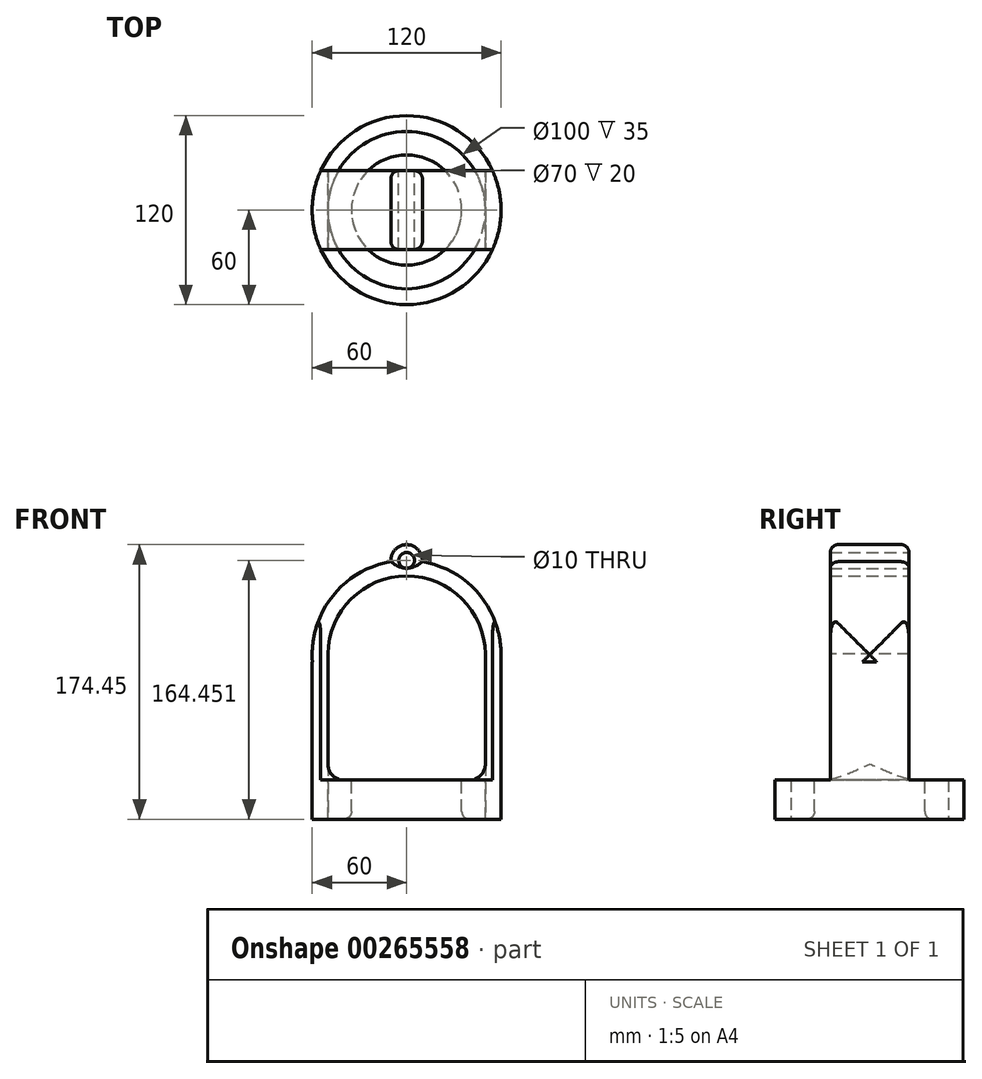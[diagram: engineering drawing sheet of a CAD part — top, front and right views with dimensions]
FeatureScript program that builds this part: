
annotation { "Feature Type Name" : "Feature", "Feature Type Description" : "" }
export const myFeature = defineFeature(function(context is Context, id is Id, definition is map)
    precondition{}
    {
        {
            var Q0;
            Q0=qCreatedBy(makeId("Top.planeOp"),FACE);
            var sketch = newSketch(context, id + "F0", { "sketchPlane" : qUnion([Q0])});
            skCircle(sketch, "E0", {"center": v(0, 0) * mm, "radius": 35 * mm});
            skCircle(sketch, "E1", {"center": v(0, 0) * mm, "radius": 50 * mm});
            skCircle(sketch, "E2", {"center": v(0, 0) * mm, "radius": 60 * mm});
            skCircle(sketch, "E3", {"center": v(0, 0) * mm, "radius": 78.9 * mm});
            skSolve(sketch);
        }
        {
            var Q0;
            Q0=qCreatedBy(makeId("Front.planeOp"),FACE);
            var sketch = newSketch(context, id + "F1", { "sketchPlane" : qUnion([Q0])});
            skLineSegment(sketch, "E4.bottom", {"start": v(-40, 0) * mm, "end": v(40, 0) * mm});
            skLineSegment(sketch, "E4.top", {"start": v(-50, 80) * mm, "end": v(50, 80) * mm});
            skLineSegment(sketch, "E4.left", {"start": v(-50, 10) * mm, "end": v(-50, 80) * mm});
            skLineSegment(sketch, "E4.right", {"start": v(50, 10) * mm, "end": v(50, 80) * mm});
            skPoint(sketch, "E5.visualSharp", {"position": v(-50, 0) * mm});
            skArc(sketch, "E5.filletArc", {"start": v(-50, 10) * mm, "mid": v(-47.07, 2.93) * mm, "end": v(-40, 0) * mm});
            skPoint(sketch, "E6.visualSharp", {"position": v(50, 0) * mm});
            skArc(sketch, "E6.filletArc", {"start": v(40, 0) * mm, "mid": v(47.07, 2.93) * mm, "end": v(50, 10) * mm});
            skPoint(sketch, "E7", {"position": v(0, 0) * mm});
            skPoint(sketch, "E8", {"position": v(0, 80) * mm});
            skSolve(sketch);
        }
        {
            var Q0;
            Q0=qCreatedBy(makeId("Front.planeOp"),FACE);
            var sketch = newSketch(context, id + "F2", { "sketchPlane" : qUnion([Q0])});
            skCircle(sketch, "E9", {"center": v(0, 79.45) * mm, "radius": 50 * mm});
            skCircle(sketch, "E10", {"center": v(0, 79.45) * mm, "radius": 60 * mm});
            skCircle(sketch, "E11", {"center": v(0, 139.45) * mm, "radius": 10 * mm});
            skCircle(sketch, "E12", {"center": v(0, 139.45) * mm, "radius": 5 * mm});
            skSolve(sketch);
        }
        {
            var Q0;
            Q0=qCreatedBy(makeId("Right.planeOp"),FACE);
            var sketch = newSketch(context, id + "F3", { "sketchPlane" : qUnion([Q0])});
            skLineSegment(sketch, "E13.bottom", {"start": v(-25, 75) * mm, "end": v(-65, 75) * mm});
            skLineSegment(sketch, "E13.top", {"start": v(-25, 0) * mm, "end": v(-65, 0) * mm});
            skLineSegment(sketch, "E13.left", {"start": v(-25, 75) * mm, "end": v(-25, 0) * mm});
            skLineSegment(sketch, "E13.right", {"start": v(-65, 75) * mm, "end": v(-65, 0) * mm});
            skLineSegment(sketch, "E14.bottom", {"start": v(65, 75) * mm, "end": v(25, 75) * mm});
            skLineSegment(sketch, "E14.top", {"start": v(65, 0) * mm, "end": v(25, 0) * mm});
            skLineSegment(sketch, "E14.left", {"start": v(65, 75) * mm, "end": v(65, 0) * mm});
            skLineSegment(sketch, "E14.right", {"start": v(25, 75) * mm, "end": v(25, 0) * mm});
            skSolve(sketch);
        }
        {
            var Q0;
            Q0=makeQuery(id+"F0.imprint","IMPRINT",FACE,{"disambiguationData":[TD([[makeQuery(id+"F0.imprint","IMPRINT",EDGE,{"derivedFrom":sQuery(id+"F0.wireOp",EDGE,"E1")}),-1.0]])]});
            extrude(context, id + "F4", {"entities" : qUnion([Q0]), "depth" : 75 * mm, "hasSecondDirection" : true, "secondDirectionOppositeDirection" : true, "secondDirectionDepth" : 25 * mm});
        }
        {
            var Q0;
            Q0=makeQuery(id+"F0.imprint","IMPRINT",FACE,{"disambiguationData":[TD([[makeQuery(id+"F0.imprint","IMPRINT",EDGE,{"derivedFrom":sQuery(id+"F0.wireOp",EDGE,"E0")}),-1.0]])]});
            extrude(context, id + "F5", {"entities" : qUnion([Q0]), "oppositeDirection" : true, "depth" : 25 * mm});
        }
        {
            var Q0;
            Q0 = qSketchRegion(id + "F1", true);
            extrude(context, id + "F6", {"entities" : qUnion([Q0]), "depth" : 25 * mm});
        }
        {
            var Q0;
            Q0=makeQuery(id+"F2.imprint","IMPRINT",FACE,{"disambiguationData":[TD([[makeQuery(id+"F2.imprint","IMPRINT",EDGE,{"derivedFrom":sQuery(id+"F2.wireOp",EDGE,"E9")}),-1.0]])]});
            var Q1;
            {var subQ0=sQuery(id+"F2.wireOp",EDGE,"E11");var subQ2=sQuery(id+"F2.wireOp",EDGE,"E10");var subQ4=makeQuery(id+"F2.imprint","INTERSECT",VERTEX,{"disambiguationData":[OD(0.0)],"derivedFrom":[subQ2,subQ0]});Q1=makeQuery(id+"F2.imprint","IMPRINT",FACE,{"disambiguationData":[TD([[makeQuery(id+"F2.imprint","IMPRINT",EDGE,{"disambiguationData":[TD([[subQ4,-1.0]])],"derivedFrom":subQ2}),1.0]])]});}
            var Q2;
            {var subQ0=sQuery(id+"F2.wireOp",EDGE,"E11");var subQ1=sQuery(id+"F2.wireOp",EDGE,"E10");var subQ2=makeQuery(id+"F2.imprint","INTERSECT",VERTEX,{"disambiguationData":[OD(0.0)],"derivedFrom":[subQ1,subQ0]});Q2=makeQuery(id+"F2.imprint","IMPRINT",FACE,{"disambiguationData":[TD([[makeQuery(id+"F2.imprint","IMPRINT",EDGE,{"disambiguationData":[TD([[subQ2,-1.0]])],"derivedFrom":subQ1}),-1.0]])]});}
            extrude(context, id + "F7", {"entities" : qUnion([Q0, Q1, Q2]), "operationType" : NewBodyOperationType.ADD, "depth" : 25 * mm, "hasSecondDirection" : true, "secondDirectionOppositeDirection" : true, "secondDirectionDepth" : 25 * mm});
        }
        {
            var Q0;
            Q0 = qSketchRegion(id + "F1", true);
            extrude(context, id + "F8", {"entities" : qUnion([Q0]), "operationType" : NewBodyOperationType.REMOVE, "oppositeDirection" : true, "depth" : 100 * mm, "hasSecondDirection" : true, "secondDirectionOppositeDirection" : false, "secondDirectionDepth" : 100 * mm});
        }
        {
            var Q0;
            Q0=makeQuery(id+"F0.imprint","IMPRINT",FACE,{"disambiguationData":[TD([[makeQuery(id+"F0.imprint","IMPRINT",EDGE,{"derivedFrom":sQuery(id+"F0.wireOp",EDGE,"E2")}),-1.0]])]});
            extrude(context, id + "F9", {"entities" : qUnion([Q0]), "operationType" : NewBodyOperationType.REMOVE, "depth" : 150 * mm});
        }
        {
            var Q0;
            Q0 = qSketchRegion(id + "F3", true);
            extrude(context, id + "F10", {"entities" : qUnion([Q0]), "operationType" : NewBodyOperationType.REMOVE, "oppositeDirection" : true, "depth" : 100 * mm, "hasSecondDirection" : true, "secondDirectionOppositeDirection" : false, "secondDirectionDepth" : 100 * mm});
        }
        {
            var Q0;
            Q0=makeQuery(id+"F7.boolean.opBoolean","SPLIT",EDGE,{"disambiguationData":[OD(0.0)],"derivedFrom":makeQuery(id+"F7.opExtrude","CAP_EDGE",EDGE,{"disambiguationData":[OSD([sQuery(id+"F2.wireOp",EDGE,"E10")])],"isStart":false})});
            var Q1;
            Q1=makeQuery(id+"F7.boolean.opBoolean","SPLIT",EDGE,{"disambiguationData":[OD(1.0)],"derivedFrom":makeQuery(id+"F7.opExtrude","CAP_EDGE",EDGE,{"disambiguationData":[OSD([sQuery(id+"F2.wireOp",EDGE,"E10")])],"isStart":false})});
            fillet(context, id + "F11", {"entities" : qUnion([Q0, Q1]), "radius" : 5 * mm, "tangentPropagation" : true, "allowEdgeOverflow" : false});
        }
        {
            var Q0;
            Q0=makeQuery(id+"F5.opExtrude","CAP_EDGE",EDGE,{"disambiguationData":[OSD([sQuery(id+"F0.wireOp",EDGE,"E0")])],"isStart":false});
            fillet(context, id + "F12", {"entities" : qUnion([Q0]), "radius" : 5 * mm, "tangentPropagation" : true, "allowEdgeOverflow" : false});
        }
        {
            var Q0;
            {var subQ0=sQuery(id+"F2.wireOp",EDGE,"E11");var subQ1=sQuery(id+"F2.wireOp",EDGE,"E10");Q0=makeQuery(id+"F7.boolean.opBoolean","SPLIT",EDGE,{"disambiguationData":[TD([makeQuery(id+"F4.opExtrude","SWEPT_FACE",FACE,{"disambiguationData":[OSD([sQuery(id+"F0.wireOp",EDGE,"E2")])]}),makeQuery(id+"F7.opExtrude","CAP_FACE",FACE,{"disambiguationData":[OSD([sQuery(id+"F2.wireOp",EDGE,"E9"),subQ1,subQ0,sQuery(id+"F2.wireOp",EDGE,"E12")])],"isStart":true}),makeQuery(id+"F7.opExtrude","SWEPT_FACE",FACE,{"disambiguationData":[OSD([subQ1])]}),makeQuery(id+"F7.opExtrude","SWEPT_FACE",FACE,{"disambiguationData":[OSD([subQ0])]})]),OD(1.0)],"derivedFrom":makeQuery(id+"F7.opExtrude","CAP_EDGE",EDGE,{"disambiguationData":[OSD([subQ1])],"isStart":true})});}
            var Q1;
            {var subQ0=sQuery(id+"F2.wireOp",EDGE,"E11");var subQ1=sQuery(id+"F2.wireOp",EDGE,"E10");Q1=makeQuery(id+"F7.boolean.opBoolean","SPLIT",EDGE,{"disambiguationData":[TD([makeQuery(id+"F4.opExtrude","SWEPT_FACE",FACE,{"disambiguationData":[OSD([sQuery(id+"F0.wireOp",EDGE,"E2")])]}),makeQuery(id+"F7.opExtrude","CAP_FACE",FACE,{"disambiguationData":[OSD([sQuery(id+"F2.wireOp",EDGE,"E9"),subQ1,subQ0,sQuery(id+"F2.wireOp",EDGE,"E12")])],"isStart":true}),makeQuery(id+"F7.opExtrude","SWEPT_FACE",FACE,{"disambiguationData":[OSD([subQ1])]}),makeQuery(id+"F7.opExtrude","SWEPT_FACE",FACE,{"disambiguationData":[OSD([subQ0])]})]),OD(0.0)],"derivedFrom":makeQuery(id+"F7.opExtrude","CAP_EDGE",EDGE,{"disambiguationData":[OSD([subQ1])],"isStart":true})});}
            var Q2;
            Q2=makeQuery(id+"F7.opExtrude","CAP_EDGE",EDGE,{"disambiguationData":[OSD([sQuery(id+"F2.wireOp",EDGE,"E11")])],"isStart":true});
            var Q3;
            Q3=makeQuery(id+"F7.opExtrude","CAP_EDGE",EDGE,{"disambiguationData":[OSD([sQuery(id+"F2.wireOp",EDGE,"E11")])],"isStart":false});
            fillet(context, id + "F13", {"entities" : qUnion([Q0, Q1, Q2, Q3]), "radius" : 5 * mm, "tangentPropagation" : true, "allowEdgeOverflow" : false});
        }
    });
